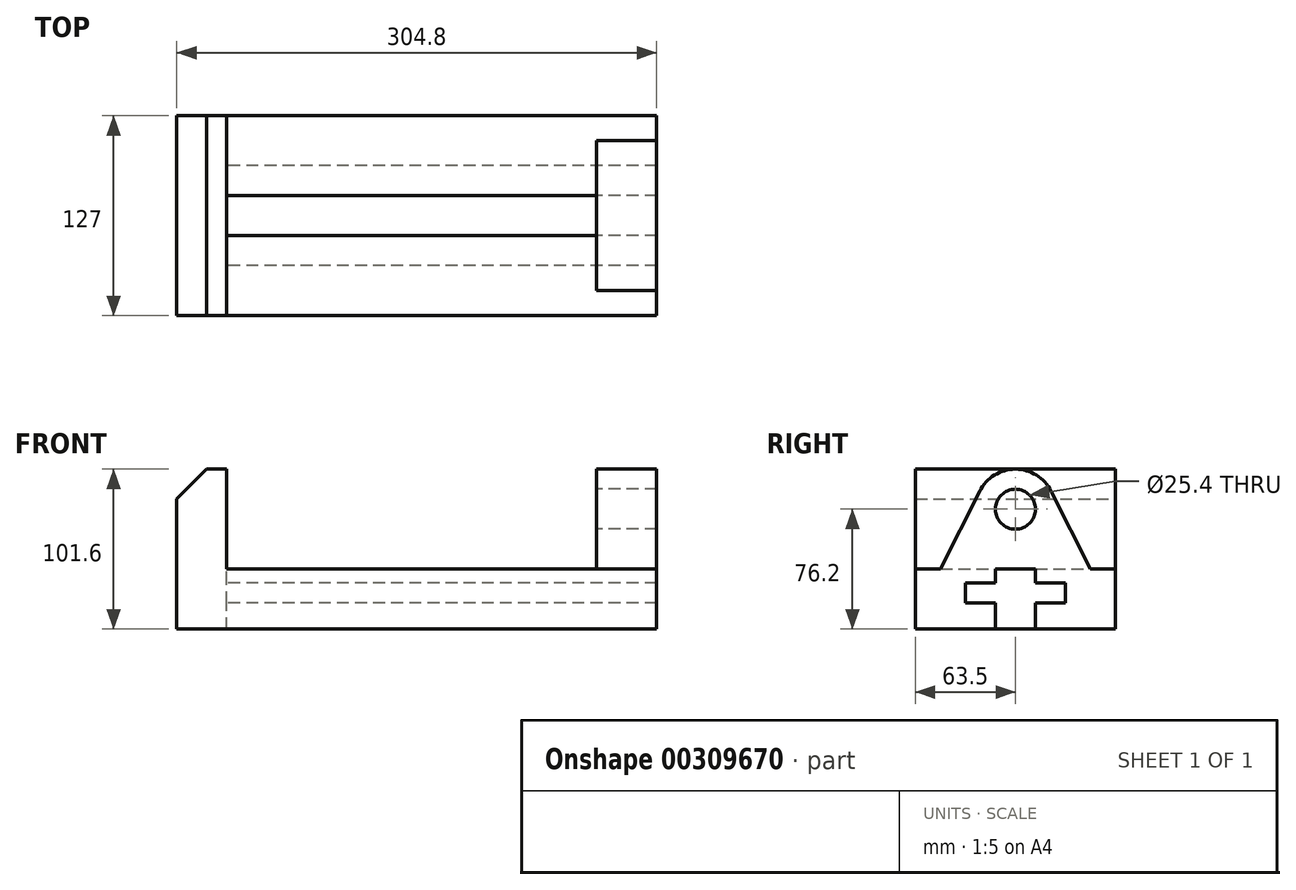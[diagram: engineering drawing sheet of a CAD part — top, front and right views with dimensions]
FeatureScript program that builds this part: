
annotation { "Feature Type Name" : "Feature", "Feature Type Description" : "" }
export const myFeature = defineFeature(function(context is Context, id is Id, definition is map)
    precondition{}
    {
        {
            var Q0;
            Q0=qCreatedBy(makeId("Front.planeOp"),FACE);
            var sketch = newSketch(context, id + "F0", { "sketchPlane" : qUnion([Q0])});
            skLineSegment(sketch, "E0", {"start": v(0, 0) * mm, "end": v(0, 82.55) * mm});
            skLineSegment(sketch, "E1", {"start": v(0, 82.55) * mm, "end": v(19.05, 101.6) * mm});
            skLineSegment(sketch, "E2", {"start": v(19.05, 101.6) * mm, "end": v(31.75, 101.6) * mm});
            skLineSegment(sketch, "E3", {"start": v(31.75, 101.6) * mm, "end": v(31.75, 0) * mm});
            skLineSegment(sketch, "E4", {"start": v(31.75, 0) * mm, "end": v(0, 0) * mm});
            skSolve(sketch);
        }
        {
            var Q0;
            Q0 = qSketchRegion(id + "F0", true);
            extrude(context, id + "F1", {"entities" : qUnion([Q0]), "depth" : 127 * mm});
        }
        {
            var Q0;
            Q0=makeQuery(id+"F1.opExtrude","SWEPT_FACE",FACE,{"disambiguationData":[OSD([sQuery(id+"F0.wireOp",EDGE,"E3")])]});
            var sketch = newSketch(context, id + "F2", { "sketchPlane" : qUnion([Q0])});
            skLineSegment(sketch, "E5", {"start": v(-127, 0) * mm, "end": v(-127, 38.1) * mm});
            skLineSegment(sketch, "E6", {"start": v(-127, 38.1) * mm, "end": v(-76.2, 38.1) * mm});
            skLineSegment(sketch, "E7", {"start": v(-76.2, 38.1) * mm, "end": v(-76.2, 29.21) * mm});
            skLineSegment(sketch, "E8", {"start": v(-76.2, 29.21) * mm, "end": v(-95.25, 29.21) * mm});
            skLineSegment(sketch, "E9", {"start": v(-95.25, 29.21) * mm, "end": v(-95.25, 16.5) * mm});
            skLineSegment(sketch, "E10", {"start": v(-95.25, 16.5) * mm, "end": v(-76.2, 16.5) * mm});
            skLineSegment(sketch, "E11", {"start": v(-76.2, 16.5) * mm, "end": v(-76.2, 0) * mm});
            skLineSegment(sketch, "E12", {"start": v(-76.2, 0) * mm, "end": v(-127, 0) * mm});
            skLineSegment(sketch, "E13", {"start": v(-50.8, 0) * mm, "end": v(-50.8, 16.5) * mm});
            skLineSegment(sketch, "E14", {"start": v(-50.8, 16.5) * mm, "end": v(-31.75, 16.51) * mm});
            skLineSegment(sketch, "E15", {"start": v(-31.75, 16.5) * mm, "end": v(-31.75, 29.21) * mm});
            skLineSegment(sketch, "E16", {"start": v(-31.75, 29.21) * mm, "end": v(-50.8, 29.21) * mm});
            skLineSegment(sketch, "E17", {"start": v(-50.8, 29.21) * mm, "end": v(-50.8, 38.1) * mm});
            skLineSegment(sketch, "E18", {"start": v(-50.8, 38.1) * mm, "end": v(0, 38.1) * mm});
            skLineSegment(sketch, "E19", {"start": v(0, 38.1) * mm, "end": v(0, 0) * mm});
            skLineSegment(sketch, "E20", {"start": v(0, 0) * mm, "end": v(-50.8, 0) * mm});
            skSolve(sketch);
        }
        {
            var Q0;
            Q0 = qSketchRegion(id + "F2", true);
            extrude(context, id + "F3", {"entities" : qUnion([Q0]), "operationType" : NewBodyOperationType.ADD, "depth" : 234.95 * mm});
        }
        {
            var Q0;
            Q0=makeQuery(id+"F3.opExtrude","CAP_FACE",FACE,{"disambiguationData":[OSD([sQuery(id+"F2.wireOp",EDGE,"E13"),sQuery(id+"F2.wireOp",EDGE,"E14"),sQuery(id+"F2.wireOp",EDGE,"E15"),sQuery(id+"F2.wireOp",EDGE,"E16"),sQuery(id+"F2.wireOp",EDGE,"E17"),sQuery(id+"F2.wireOp",EDGE,"E18"),sQuery(id+"F2.wireOp",EDGE,"E19"),sQuery(id+"F2.wireOp",EDGE,"E20")])],"isStart":false});
            var sketch = newSketch(context, id + "F4", { "sketchPlane" : qUnion([Q0])});
            skLineSegment(sketch, "E21", {"start": v(-127, 0) * mm, "end": v(-127, 38.1) * mm});
            skLineSegment(sketch, "E22", {"start": v(-127, 38.1) * mm, "end": v(-111.12, 38.1) * mm});
            skLineSegment(sketch, "E23", {"start": v(-15.88, 38.1) * mm, "end": v(0, 38.1) * mm});
            skLineSegment(sketch, "E24", {"start": v(0, 38.1) * mm, "end": v(0, 0) * mm});
            skLineSegment(sketch, "E25", {"start": v(0, 0) * mm, "end": v(-50.8, 0) * mm});
            skLineSegment(sketch, "E26", {"start": v(-50.8, 0) * mm, "end": v(-50.8, 16.5) * mm});
            skLineSegment(sketch, "E27", {"start": v(-50.8, 16.5) * mm, "end": v(-31.75, 16.5) * mm});
            skLineSegment(sketch, "E28", {"start": v(-31.75, 16.5) * mm, "end": v(-31.75, 29.21) * mm});
            skLineSegment(sketch, "E29", {"start": v(-31.75, 29.21) * mm, "end": v(-50.8, 29.21) * mm});
            skLineSegment(sketch, "E30", {"start": v(-50.8, 29.21) * mm, "end": v(-50.8, 38.1) * mm});
            skLineSegment(sketch, "E31", {"start": v(-50.8, 38.1) * mm, "end": v(-76.2, 38.1) * mm});
            skLineSegment(sketch, "E32", {"start": v(-76.2, 38.1) * mm, "end": v(-76.2, 29.21) * mm});
            skLineSegment(sketch, "E33", {"start": v(-76.2, 29.21) * mm, "end": v(-95.25, 29.21) * mm});
            skLineSegment(sketch, "E34", {"start": v(-95.25, 29.21) * mm, "end": v(-95.25, 16.5) * mm});
            skLineSegment(sketch, "E35", {"start": v(-95.25, 16.5) * mm, "end": v(-76.2, 16.5) * mm});
            skLineSegment(sketch, "E36", {"start": v(-76.2, 16.5) * mm, "end": v(-76.2, 0) * mm});
            skLineSegment(sketch, "E37", {"start": v(-76.2, 0) * mm, "end": v(-127, 0) * mm});
            skLineSegment(sketch, "E38", {"start": v(-76.2, 0) * mm, "end": v(-50.8, 0) * mm, "construction": true});
            skLineSegment(sketch, "E39", {"start": v(-63.5, 0) * mm, "end": v(-63.5, 76.2) * mm, "construction": true});
            skCircle(sketch, "E40", {"center": v(-63.5, 76.2) * mm, "radius": 12.7 * mm});
            skLineSegment(sketch, "E41", {"start": v(-111.12, 38.1) * mm, "end": v(-86.19, 87.62) * mm});
            skLineSegment(sketch, "E42", {"start": v(-15.88, 38.1) * mm, "end": v(-40.81, 87.62) * mm});
            skArc(sketch, "E43", {"start": v(-40.81, 87.62) * mm, "mid": v(-63.5, 101.6) * mm, "end": v(-86.19, 87.62) * mm});
            skSolve(sketch);
        }
        {
            var Q0;
            Q0 = qSketchRegion(id + "F4", true);
            extrude(context, id + "F5", {"entities" : qUnion([Q0]), "operationType" : NewBodyOperationType.ADD, "depth" : 38.1 * mm});
        }
    });
